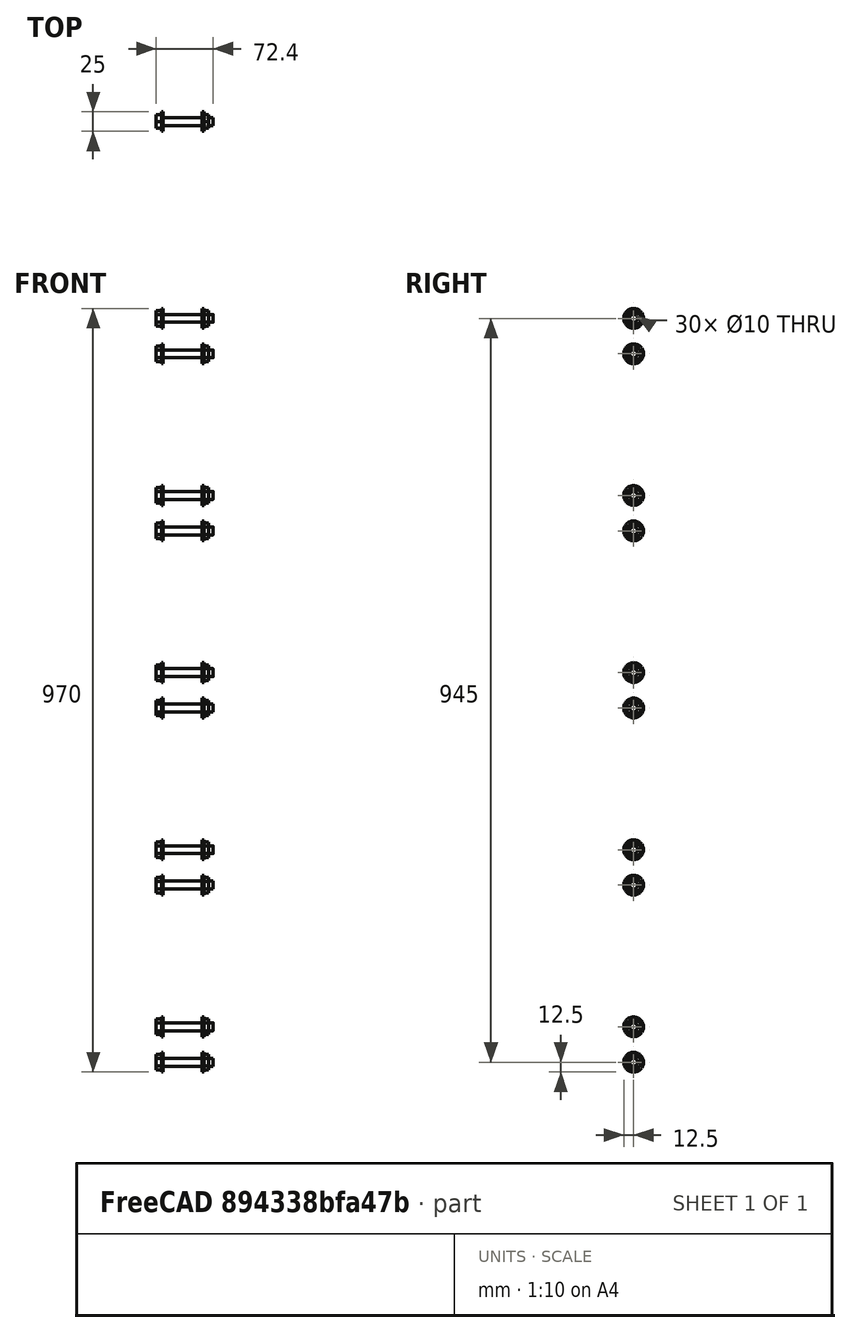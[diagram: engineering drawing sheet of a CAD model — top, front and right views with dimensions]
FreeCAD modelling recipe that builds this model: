
FCSTD DOCUMENT  (FreeCAD 0.17R10993 (Git))
Label: railing_fasteners
License: All rights reserved
LicenseURL: http://en.wikipedia.org/wiki/All_rights_reserved
objects: Part::FeaturePython×3, Part::Part2DObjectPython×2, Part::Extrusion×2, Part::Cut×1, Part::Feature×1, Part::Compound×1
note: 10 computed .brp shape members not serialized (recipe doc carries the construction recipe); baked Part::Feature solids carry a one-line shape summary decoded from their .brp

FEATURE [Part::Part2DObjectPython] Circle003  # Draft 2D object (typed FeaturePython)
  FirstAngle = 0
  LastAngle = 0
  MakeFace = true
  Placement = pos=(32.2,-375,44) rot=(1,0,0;1.5708rad)
  Radius = 12.5
FEATURE [Part::Extrusion] Extrude006
  Base = -> Circle003
  Dir = (0,-1,0)
  DirMode = 0
  FaceMakerClass = Part::FaceMakerBullseye
  LengthFwd = 2
  LengthRev = 0
  Solid = false
  Symmetric = false
FEATURE [Part::Part2DObjectPython] Circle004  # Draft 2D object (typed FeaturePython)
  FirstAngle = 0
  LastAngle = 0
  MakeFace = true
  Placement = pos=(32.2,-375,44) rot=(1,0,0;1.5708rad)
  Radius = 5
FEATURE [Part::Extrusion] Extrude007
  Base = -> Circle004
  Dir = (0,-1,0)
  DirMode = 0
  FaceMakerClass = Part::FaceMakerBullseye
  LengthFwd = 2
  LengthRev = 0
  Solid = false
  Symmetric = false
FEATURE [Part::Cut] Cut004  label="washer"
  Base = -> Extrude006
  Tool = -> Extrude007
FEATURE [Part::FeaturePython] Component002  label="washer003"  # WARN: FeaturePython — macro-defined, semantics opaque (R4)
  CloneOf = -> Cut004
  HorizontalArea = 0
  MoveWithHost = false
  PerimeterLength = 0
  Placement = pos=(0,52,0) rot=(0,0,1;0rad)
  Role = 0
  VerticalArea = 0
FEATURE [Part::FeaturePython] Component003  label="nuts001"  # WARN: FeaturePython — macro-defined, semantics opaque (R4)
  HorizontalArea = 0
  MoveWithHost = false
  PerimeterLength = 0
  Placement = pos=(32.2,-317,44) rot=(1,0,0;1.5708rad)
  Role = 0
  VerticalArea = 0
FEATURE [Part::Feature] BOLTS_part  label="Hexagon head bolt DIN 931 M10 - 66.0"
  Placement = pos=(32.2,-383.4,44) rot=(-1,0,0;1.5708rad)
  shape: bbox 17 x 72.4 x 19.63 mm, 11 faces (baked)
FEATURE [Part::Compound] Compound004  label="fastener_and_nuts"
  Links = -> [Cut004,Component003,Component002,BOLTS_part]
  Placement = pos=(439.39,-378.8,28.5) rot=(0,0,-1;1.5708rad)
FEATURE [Part::FeaturePython] Array006  label="railing_fastener"  # Draft array (typed FeaturePython)
  Angle = 360
  ArrayType = 0
  Axis = (0,0,1)
  Base = -> Compound004
  Center = (0,0,0)
  Fuse = false
  IntervalAxis = (0,0,0)
  IntervalX = (0,0,45)
  IntervalY = (0,0,225)
  IntervalZ = (630,0,615)
  NumberPolar = 1
  NumberX = 2
  NumberY = 5
  NumberZ = 0
